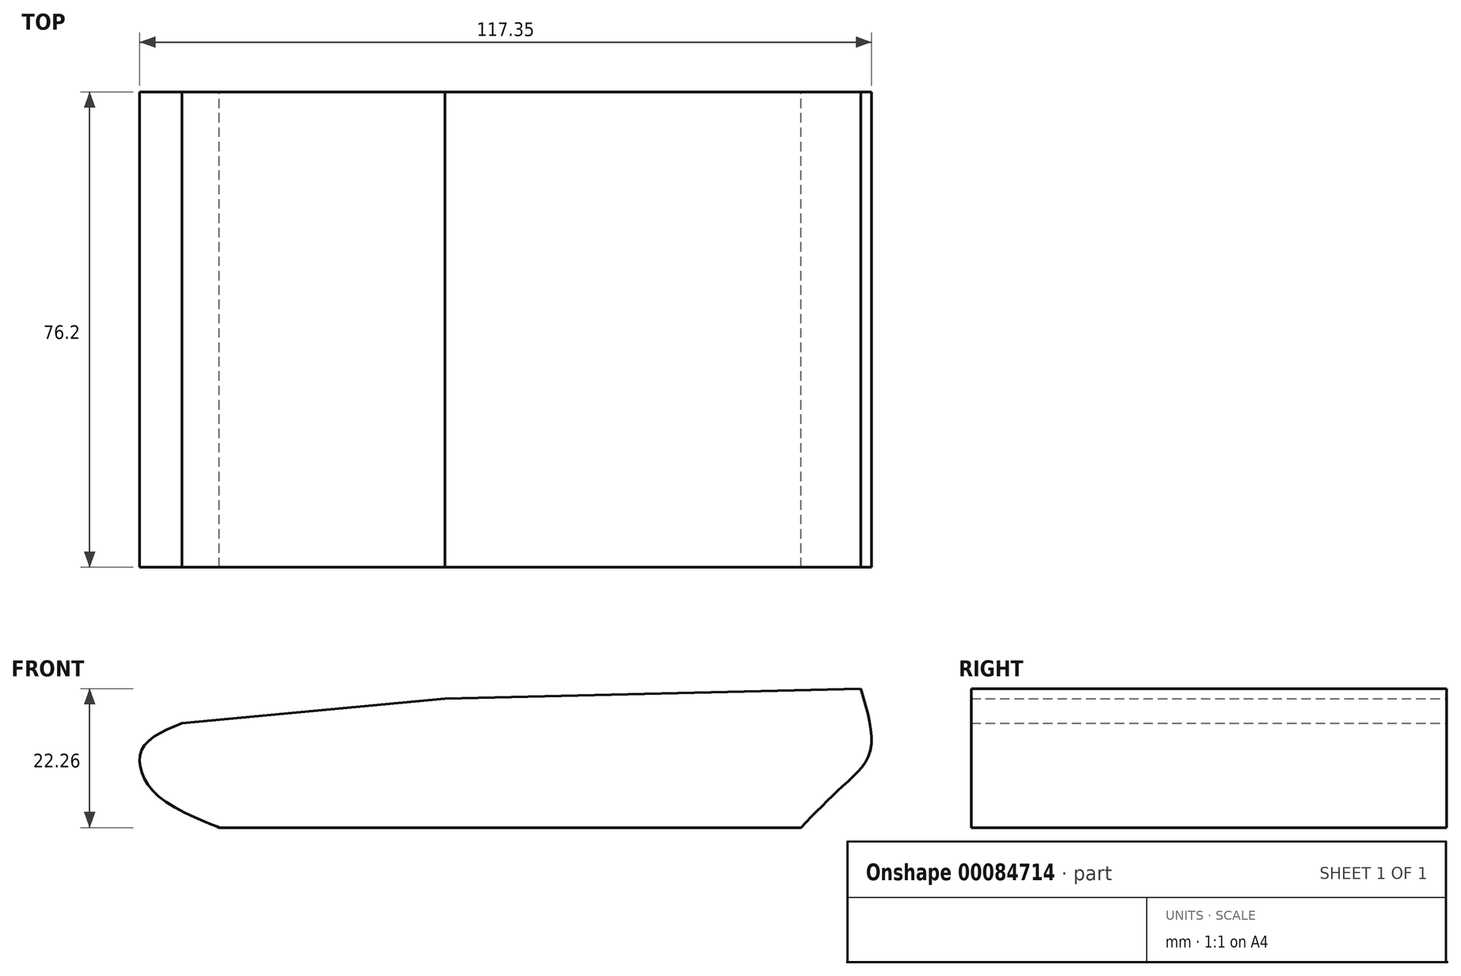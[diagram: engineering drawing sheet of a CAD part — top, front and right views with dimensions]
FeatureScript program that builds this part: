
annotation { "Feature Type Name" : "Feature", "Feature Type Description" : "" }
export const myFeature = defineFeature(function(context is Context, id is Id, definition is map)
    precondition{}
    {
        {
            var Q0;
            Q0=qCreatedBy(makeId("Front.planeOp"),FACE);
            var sketch = newSketch(context, id + "F0", { "sketchPlane" : qUnion([Q0])});
            skLineSegment(sketch, "E0", {"start": v(-23.44, 0) * mm, "end": v(-65.6, -3.92) * mm});
            skFitSpline(sketch, "E1", {"points": [v(-65.6, -3.92) * mm, v(-71.56, -7.4) * mm, v(-72.23, -11.23) * mm, v(-67.7, -16.88) * mm, v(-59.66, -20.67) * mm, v(-59.74, -20.67) * mm], "startDerivative": vector(-29.1, -12.18) * mm, "endDerivative": vector(-4.67, 0.56) * mm});
            skLineSegment(sketch, "E2", {"start": v(-59.66, -20.67) * mm, "end": v(33.64, -20.67) * mm});
            skFitSpline(sketch, "E3", {"points": [v(33.64, -20.67) * mm, v(40.2, -14.14) * mm, v(44.71, -8.53) * mm, v(43.22, 1.6) * mm], "startDerivative": vector(19.2, 19.92) * mm, "endDerivative": vector(-9.38, 31.04) * mm});
            skLineSegment(sketch, "E4", {"start": v(43.22, 1.6) * mm, "end": v(-23.44, 0) * mm});
            skSolve(sketch);
        }
        {
            var Q0;
            {var subQ2=sQuery(id+"F0.wireOp",EDGE,"E0");Q0=makeQuery(id+"F0.imprint","IMPRINT",FACE,{"disambiguationData":[TD([[makeQuery(id+"F0.imprint","IMPRINT",EDGE,{"derivedFrom":subQ2}),1.0]])]});}
            extrude(context, id + "F1", {"entities" : qUnion([Q0]), "endBound" : BoundingType.SYMMETRIC, "depth" : 76.2 * mm});
        }
    });
